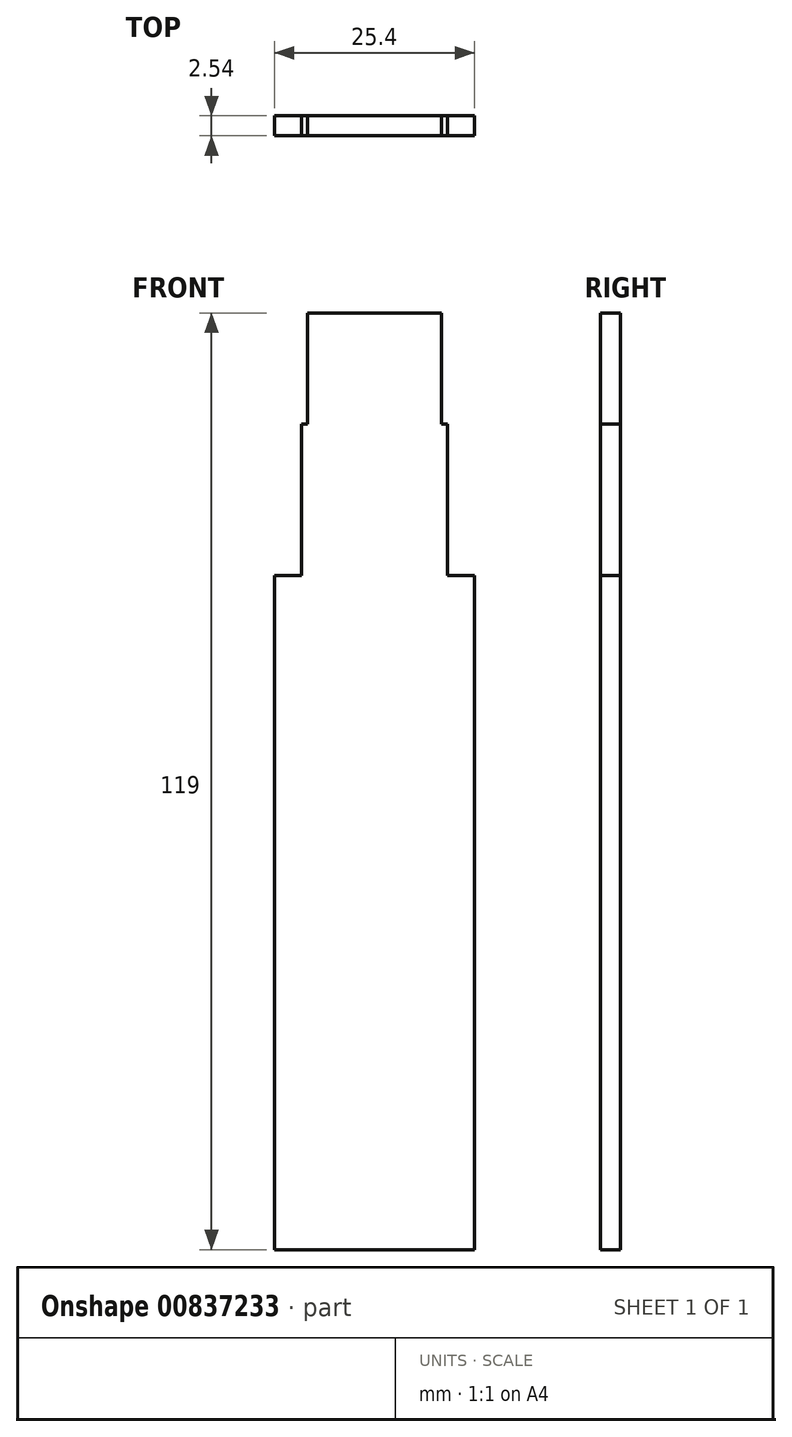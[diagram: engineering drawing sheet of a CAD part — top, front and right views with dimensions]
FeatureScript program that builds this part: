
annotation { "Feature Type Name" : "Feature", "Feature Type Description" : "" }
export const myFeature = defineFeature(function(context is Context, id is Id, definition is map)
    precondition{}
    {
        {
            var Q0;
            Q0=qCreatedBy(makeId("Front.planeOp"),FACE);
            var sketch = newSketch(context, id + "F0", { "sketchPlane" : qUnion([Q0])});
            skLineSegment(sketch, "E0", {"start": v(0, 0) * mm, "end": v(-12.7, 0) * mm});
            skLineSegment(sketch, "E1.MirrorCS", {"start": v(0, 0) * mm, "end": v(12.7, 0) * mm});
            skLineSegment(sketch, "E2", {"start": v(-12.7, 0) * mm, "end": v(-12.7, 85.67) * mm});
            skLineSegment(sketch, "E3", {"start": v(-8.5, 119) * mm, "end": v(8.5, 119) * mm});
            skLineSegment(sketch, "E4", {"start": v(12.7, 85.67) * mm, "end": v(12.7, 0) * mm});
            skLineSegment(sketch, "E5", {"start": v(-9.3, 94.91) * mm, "end": v(9.3, 94.91) * mm});
            skLineSegment(sketch, "E6", {"start": v(-9.3, 104.9) * mm, "end": v(9.3, 104.9) * mm});
            skLineSegment(sketch, "E7", {"start": v(-8.5, 104.9) * mm, "end": v(-8.5, 119) * mm});
            skLineSegment(sketch, "E8", {"start": v(8.5, 119) * mm, "end": v(8.5, 104.9) * mm});
            skLineSegment(sketch, "E9", {"start": v(8.5, 104.9) * mm, "end": v(-8.5, 104.9) * mm});
            skLineSegment(sketch, "E10", {"start": v(-12.7, 85.67) * mm, "end": v(12.7, 85.67) * mm});
            skLineSegment(sketch, "E11", {"start": v(-9.3, 85.67) * mm, "end": v(-9.3, 104.9) * mm});
            skLineSegment(sketch, "E12", {"start": v(9.3, 85.67) * mm, "end": v(9.3, 104.9) * mm});
            skSolve(sketch);
        }
        {
            var Q0;
            Q0=makeQuery(id+"F0.imprint","IMPRINT",FACE,{"disambiguationData":[TD([[makeQuery(id+"F0.imprint","IMPRINT",EDGE,{"derivedFrom":sQuery(id+"F0.wireOp",EDGE,"E0")}),-1.0]])]});
            var Q1;
            {var subQ0=sQuery(id+"F0.wireOp",EDGE,"E5");Q1=makeQuery(id+"F0.imprint","IMPRINT",FACE,{"disambiguationData":[TD([[makeQuery(id+"F0.imprint","IMPRINT",EDGE,{"derivedFrom":subQ0}),-1.0]])]});}
            var Q2;
            {var subQ7=sQuery(id+"F0.wireOp",EDGE,"E5");Q2=makeQuery(id+"F0.imprint","IMPRINT",FACE,{"disambiguationData":[TD([[makeQuery(id+"F0.imprint","IMPRINT",EDGE,{"derivedFrom":subQ7}),1.0]])]});}
            var Q3;
            Q3=makeQuery(id+"F0.imprint","IMPRINT",FACE,{"disambiguationData":[TD([[makeQuery(id+"F0.imprint","IMPRINT",EDGE,{"derivedFrom":sQuery(id+"F0.wireOp",EDGE,"E3")}),-1.0]])]});
            extrude(context, id + "F1", {"entities" : qUnion([Q0, Q1, Q2, Q3]), "oppositeDirection" : true, "depth" : 2.54 * mm, "offsetDistance" : 25.4 * mm});
        }
    });
